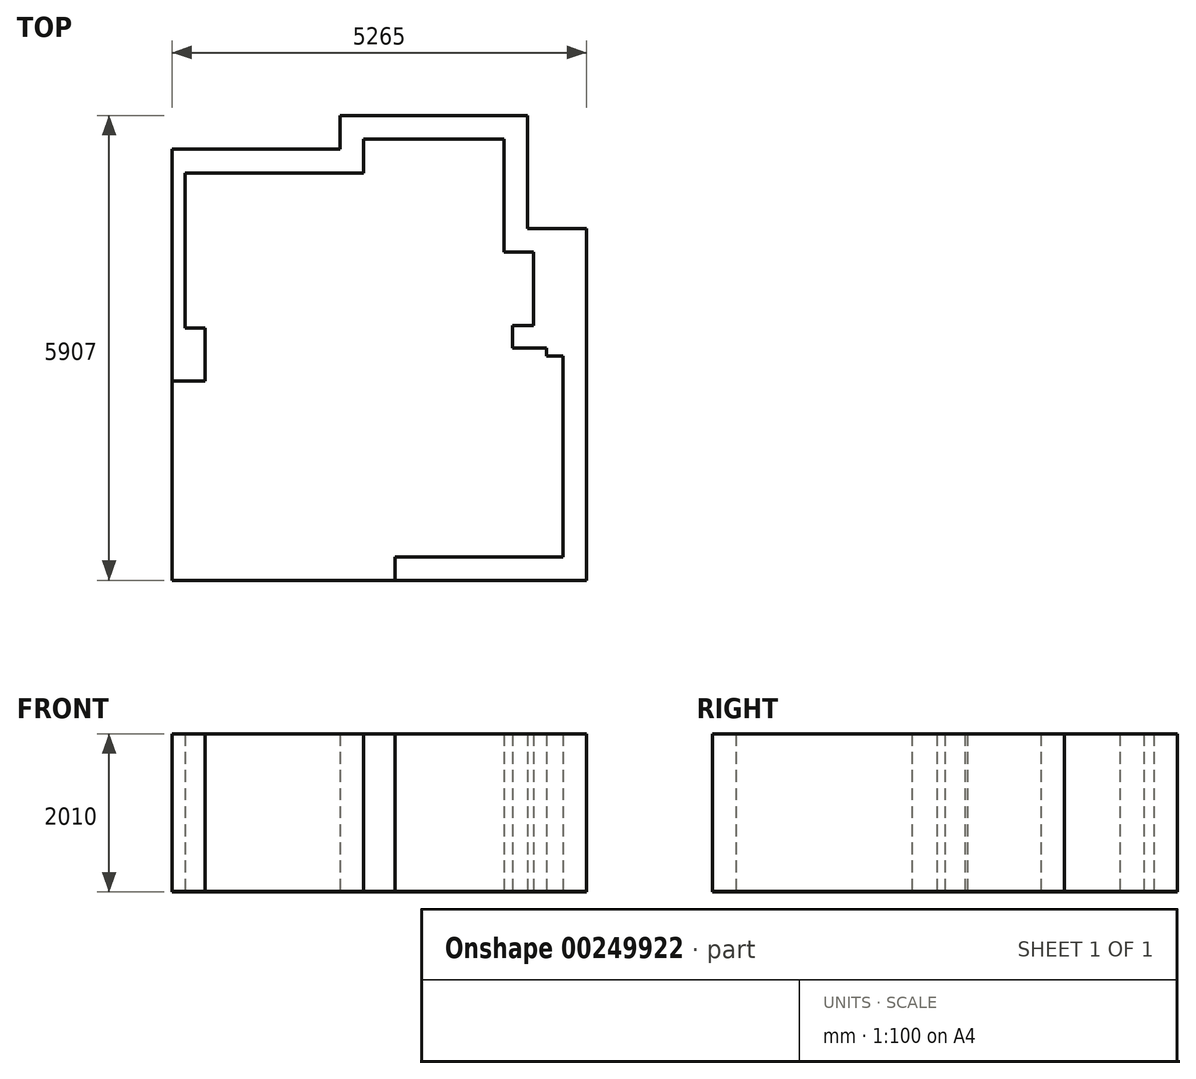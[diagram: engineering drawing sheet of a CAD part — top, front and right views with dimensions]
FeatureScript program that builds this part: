
annotation { "Feature Type Name" : "Feature", "Feature Type Description" : "" }
export const myFeature = defineFeature(function(context is Context, id is Id, definition is map)
    precondition{}
    {
        {
            var Q0;
            Q0=qCreatedBy(makeId("Top.planeOp"),FACE);
            var sketch = newSketch(context, id + "F0", { "sketchPlane" : qUnion([Q0])});
            skLineSegment(sketch, "E0", {"start": v(0, 0) * mm, "end": v(0, 2945) * mm});
            skLineSegment(sketch, "E1", {"start": v(0, 0) * mm, "end": v(420, 0) * mm});
            skLineSegment(sketch, "E2", {"start": v(420, 0) * mm, "end": v(420, 675) * mm});
            skLineSegment(sketch, "E3", {"start": v(420, 675) * mm, "end": v(165, 675) * mm});
            skLineSegment(sketch, "E4", {"start": v(165, 675) * mm, "end": v(165, 2645) * mm});
            skLineSegment(sketch, "E5", {"start": v(165, 2645) * mm, "end": v(2435, 2645) * mm});
            skLineSegment(sketch, "E6", {"start": v(2435, 2645) * mm, "end": v(2435, 3075) * mm});
            skLineSegment(sketch, "E7", {"start": v(2435, 3075) * mm, "end": v(4215, 3075) * mm});
            skLineSegment(sketch, "E8", {"start": v(4215, 3075) * mm, "end": v(4215, 1640) * mm});
            skLineSegment(sketch, "E9", {"start": v(4215, 1640) * mm, "end": v(4590, 1640) * mm});
            skLineSegment(sketch, "E10", {"start": v(4590, 1640) * mm, "end": v(4590, 705) * mm});
            skLineSegment(sketch, "E11", {"start": v(4590, 705) * mm, "end": v(4325, 705) * mm});
            skLineSegment(sketch, "E12", {"start": v(4325, 705) * mm, "end": v(4325, 420) * mm});
            skLineSegment(sketch, "E13", {"start": v(4325, 420) * mm, "end": v(4755, 420) * mm});
            skLineSegment(sketch, "E14", {"start": v(4755, 420) * mm, "end": v(4755, 320) * mm});
            skLineSegment(sketch, "E15", {"start": v(4755, 320) * mm, "end": v(4965, 320) * mm});
            skLineSegment(sketch, "E16", {"start": v(4965, 320) * mm, "end": v(4965, -2232) * mm});
            skLineSegment(sketch, "E17", {"start": v(4965, -2232) * mm, "end": v(2832, -2232) * mm});
            skLineSegment(sketch, "E18", {"start": v(2832, -2232) * mm, "end": v(2832, -2532) * mm});
            skLineSegment(sketch, "E19", {"start": v(2832, -2532) * mm, "end": v(5265, -2532) * mm});
            skLineSegment(sketch, "E20", {"start": v(5265, -2532) * mm, "end": v(5265, 1940) * mm});
            skLineSegment(sketch, "E21", {"start": v(5265, 1940) * mm, "end": v(4515, 1940) * mm});
            skLineSegment(sketch, "E22", {"start": v(4515, 1940) * mm, "end": v(4515, 3375) * mm});
            skLineSegment(sketch, "E23", {"start": v(4515, 3375) * mm, "end": v(2135, 3375) * mm});
            skLineSegment(sketch, "E24", {"start": v(2135, 3375) * mm, "end": v(2135, 2945) * mm});
            skLineSegment(sketch, "E25", {"start": v(2135, 2945) * mm, "end": v(0, 2945) * mm});
            skLineSegment(sketch, "E26", {"start": v(0, 0) * mm, "end": v(0, -2532) * mm});
            skLineSegment(sketch, "E27", {"start": v(0, -2532) * mm, "end": v(2832, -2532) * mm});
            skSolve(sketch);
        }
        {
            var Q0;
            Q0=makeQuery(id+"F0.imprint","IMPRINT",FACE,{"disambiguationData":[TD([[makeQuery(id+"F0.imprint","IMPRINT",EDGE,{"derivedFrom":sQuery(id+"F0.wireOp",EDGE,"E0")}),-1.0]])]});
            extrude(context, id + "F1", {"entities" : qUnion([Q0]), "depth" : 2000 * mm});
        }
        {
            var Q0;
            Q0 = qSketchRegion(id + "F0", true);
            extrude(context, id + "F2", {"entities" : qUnion([Q0]), "oppositeDirection" : true, "depth" : 10 * mm});
        }
    });
